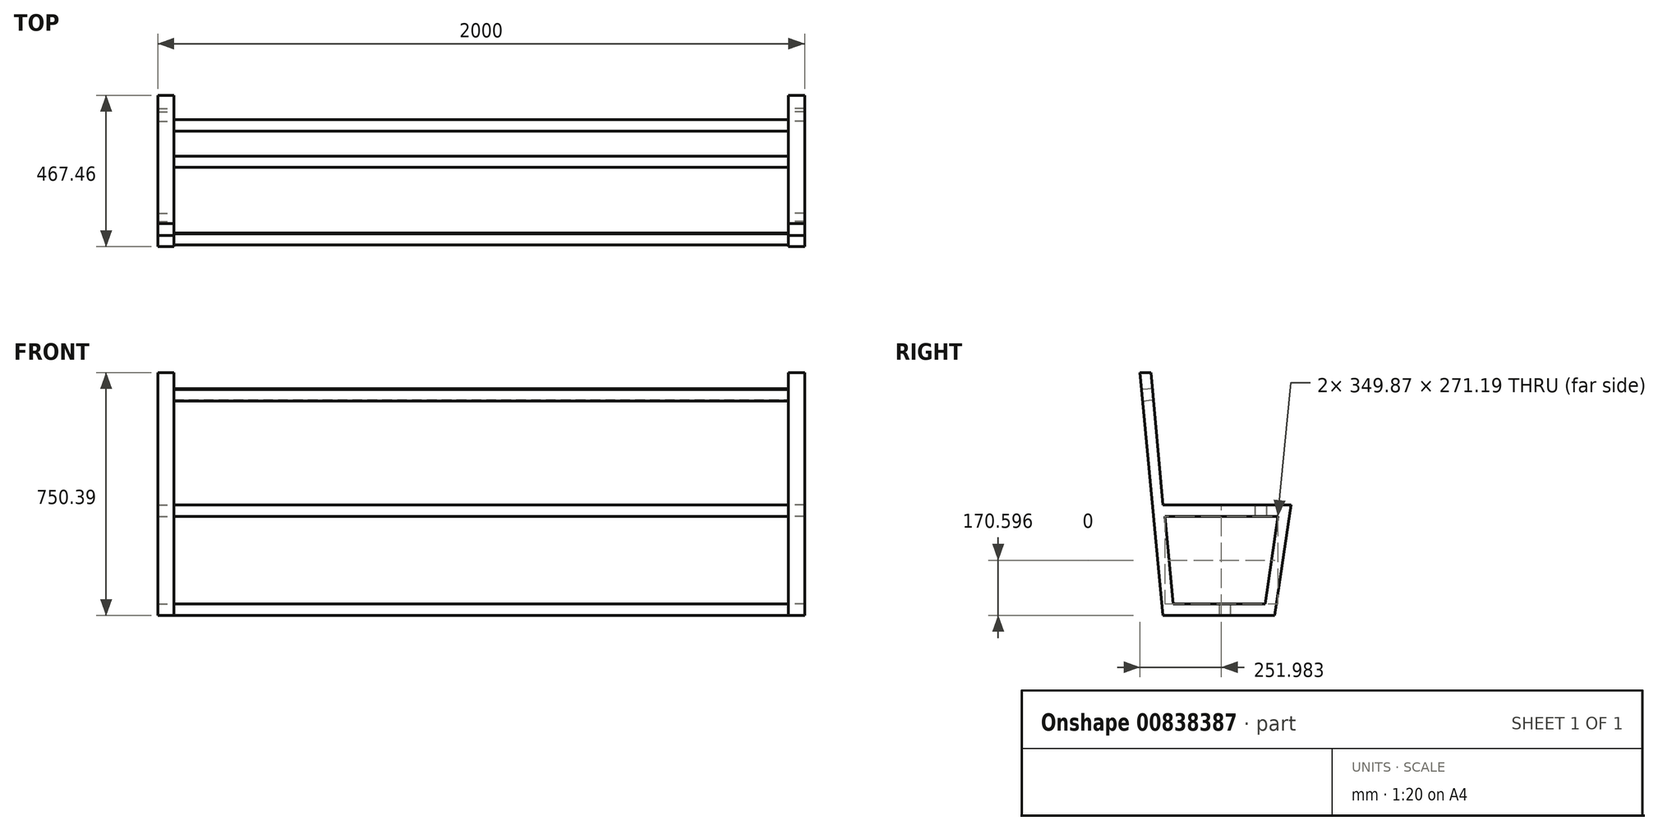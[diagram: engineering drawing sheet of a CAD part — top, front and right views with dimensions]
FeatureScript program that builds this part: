
annotation { "Feature Type Name" : "Feature", "Feature Type Description" : "" }
export const myFeature = defineFeature(function(context is Context, id is Id, definition is map)
    precondition{}
    {
        {
            var Q0;
            Q0=qCreatedBy(makeId("Right.planeOp"),FACE);
            var sketch = newSketch(context, id + "F0", { "sketchPlane" : qUnion([Q0])});
            skLineSegment(sketch, "E0.top", {"start": v(32.57, 750.39) * mm, "end": v(66.99, 750.39) * mm});
            skLineSegment(sketch, "E1", {"start": v(66.99, 750.39) * mm, "end": v(103.34, 341.2) * mm});
            skLineSegment(sketch, "E2", {"start": v(103.34, 341.2) * mm, "end": v(500.03, 341.2) * mm});
            skLineSegment(sketch, "E3", {"start": v(32.57, 750.39) * mm, "end": v(103.34, 0) * mm});
            skLineSegment(sketch, "E4", {"start": v(103.34, 0) * mm, "end": v(449.66, 0) * mm});
            skLineSegment(sketch, "E5", {"start": v(449.66, 0) * mm, "end": v(500.03, 341.2) * mm});
            skLineSegment(sketch, "E6", {"start": v(135.2, 35) * mm, "end": v(419.45, 35) * mm});
            skLineSegment(sketch, "E7", {"start": v(419.45, 35) * mm, "end": v(459.49, 306.2) * mm});
            skLineSegment(sketch, "E8", {"start": v(459.49, 306.2) * mm, "end": v(109.62, 306.2) * mm});
            skLineSegment(sketch, "E9", {"start": v(109.62, 306.2) * mm, "end": v(135.2, 35) * mm});
            skSolve(sketch);
        }
        {
            var Q0;
            Q0 = qSketchRegion(id + "F0", true);
            extrude(context, id + "F1", {"entities" : qUnion([Q0]), "depth" : 50 * mm, "offsetDistance" : 25 * mm});
        }
        {
            var Q0;
            Q0=makeQuery(id+"F1.opExtrude","CAP_FACE",FACE,{"disambiguationData":[OSD([sQuery(id+"F0.wireOp",EDGE,"E0.top"),sQuery(id+"F0.wireOp",EDGE,"E1"),sQuery(id+"F0.wireOp",EDGE,"E2"),sQuery(id+"F0.wireOp",EDGE,"E3"),sQuery(id+"F0.wireOp",EDGE,"E4"),sQuery(id+"F0.wireOp",EDGE,"E5"),sQuery(id+"F0.wireOp",EDGE,"E6"),sQuery(id+"F0.wireOp",EDGE,"E7"),sQuery(id+"F0.wireOp",EDGE,"E8"),sQuery(id+"F0.wireOp",EDGE,"E9")])],"isStart":true});
            var sketch = newSketch(context, id + "F2", { "sketchPlane" : qUnion([Q0])});
            skLineSegment(sketch, "E10.bottom", {"start": v(-284.55, 306.2) * mm, "end": v(-319.55, 306.2) * mm});
            skLineSegment(sketch, "E10.top", {"start": v(-284.55, 341.2) * mm, "end": v(-319.55, 341.2) * mm});
            skLineSegment(sketch, "E10.left", {"start": v(-284.55, 306.2) * mm, "end": v(-284.55, 341.2) * mm});
            skLineSegment(sketch, "E10.right", {"start": v(-319.55, 306.2) * mm, "end": v(-319.55, 341.2) * mm});
            skLineSegment(sketch, "E11.bottom", {"start": v(-277.32, 35) * mm, "end": v(-312.32, 35) * mm});
            skLineSegment(sketch, "E11.top", {"start": v(-277.32, 0) * mm, "end": v(-312.32, 0) * mm});
            skLineSegment(sketch, "E11.left", {"start": v(-277.32, 35) * mm, "end": v(-277.32, 0) * mm});
            skLineSegment(sketch, "E11.right", {"start": v(-312.32, 35) * mm, "end": v(-312.32, 0) * mm});
            skSolve(sketch);
        }
        {
            var Q0;
            Q0 = qSketchRegion(id + "F2", true);
            extrude(context, id + "F3", {"entities" : qUnion([Q0]), "depth" : 950 * mm, "offsetDistance" : 25 * mm});
        }
        {
            var Q0;
            Q0=makeQuery(id+"F1.opExtrude","SWEPT_BODY",BODY,{"disambiguationData":[OSD([sQuery(id+"F0.wireOp",EDGE,"E0.top"),sQuery(id+"F0.wireOp",EDGE,"E1"),sQuery(id+"F0.wireOp",EDGE,"E2"),sQuery(id+"F0.wireOp",EDGE,"E3"),sQuery(id+"F0.wireOp",EDGE,"E4"),sQuery(id+"F0.wireOp",EDGE,"E5"),sQuery(id+"F0.wireOp",EDGE,"E6"),sQuery(id+"F0.wireOp",EDGE,"E7"),sQuery(id+"F0.wireOp",EDGE,"E8"),sQuery(id+"F0.wireOp",EDGE,"E9")])]});
            var Q1;
            Q1=makeQuery(id+"F3.opExtrude","CAP_FACE",FACE,{"disambiguationData":[OSD([sQuery(id+"F2.wireOp",EDGE,"E10.bottom"),sQuery(id+"F2.wireOp",EDGE,"E10.top"),sQuery(id+"F2.wireOp",EDGE,"E10.left"),sQuery(id+"F2.wireOp",EDGE,"E10.right")])],"isStart":false});
            mirror(context, id + "F4", {"entities" : qUnion([Q0]), "mirrorPlane" : qUnion([Q1])});
        }
        {
            var Q0;
            Q0=makeQuery(id+"F3.opExtrude","SWEPT_BODY",BODY,{"disambiguationData":[OSD([sQuery(id+"F2.wireOp",EDGE,"E11.bottom"),sQuery(id+"F2.wireOp",EDGE,"E11.top"),sQuery(id+"F2.wireOp",EDGE,"E11.left"),sQuery(id+"F2.wireOp",EDGE,"E11.right")])]});
            var Q1;
            Q1=makeQuery(id+"F3.opExtrude","SWEPT_BODY",BODY,{"disambiguationData":[OSD([sQuery(id+"F2.wireOp",EDGE,"E10.bottom"),sQuery(id+"F2.wireOp",EDGE,"E10.top"),sQuery(id+"F2.wireOp",EDGE,"E10.left"),sQuery(id+"F2.wireOp",EDGE,"E10.right")])]});
            deleteBodies(context, id + "F5", {"entities" : qUnion([Q0, Q1])});
        }
        {
            var Q0;
            Q0=makeQuery(id+"F1.opExtrude","CAP_FACE",FACE,{"disambiguationData":[OSD([sQuery(id+"F0.wireOp",EDGE,"E0.top"),sQuery(id+"F0.wireOp",EDGE,"E1"),sQuery(id+"F0.wireOp",EDGE,"E2"),sQuery(id+"F0.wireOp",EDGE,"E3"),sQuery(id+"F0.wireOp",EDGE,"E4"),sQuery(id+"F0.wireOp",EDGE,"E5"),sQuery(id+"F0.wireOp",EDGE,"E6"),sQuery(id+"F0.wireOp",EDGE,"E7"),sQuery(id+"F0.wireOp",EDGE,"E8"),sQuery(id+"F0.wireOp",EDGE,"E9")])],"isStart":true});
            var sketch = newSketch(context, id + "F6", { "sketchPlane" : qUnion([Q0])});
            skLineSegment(sketch, "E12.bottom", {"start": v(-277.32, 35) * mm, "end": v(-312.32, 35) * mm});
            skLineSegment(sketch, "E12.top", {"start": v(-277.32, 0) * mm, "end": v(-312.32, 0) * mm});
            skLineSegment(sketch, "E12.left", {"start": v(-277.32, 35) * mm, "end": v(-277.32, 0) * mm});
            skLineSegment(sketch, "E12.right", {"start": v(-312.32, 35) * mm, "end": v(-312.32, 0) * mm});
            skLineSegment(sketch, "E13", {"start": v(-71.37, 701.06) * mm, "end": v(-37.5, 698.05) * mm});
            skLineSegment(sketch, "E14", {"start": v(-37.5, 698.05) * mm, "end": v(-40.8, 663.2) * mm});
            skLineSegment(sketch, "E15", {"start": v(-40.8, 663.2) * mm, "end": v(-74.45, 666.38) * mm});
            skLineSegment(sketch, "E16", {"start": v(-74.45, 666.38) * mm, "end": v(-71.37, 701.06) * mm});
            skLineSegment(sketch, "E17.bottom", {"start": v(-424.8, 306.2) * mm, "end": v(-389.8, 306.2) * mm});
            skLineSegment(sketch, "E17.top", {"start": v(-424.8, 341.2) * mm, "end": v(-389.8, 341.2) * mm});
            skLineSegment(sketch, "E17.left", {"start": v(-424.8, 306.2) * mm, "end": v(-424.8, 341.2) * mm});
            skLineSegment(sketch, "E17.right", {"start": v(-389.8, 306.2) * mm, "end": v(-389.8, 341.2) * mm});
            skSolve(sketch);
        }
        {
            var Q0;
            Q0 = qSketchRegion(id + "F6", true);
            extrude(context, id + "F7", {"entities" : qUnion([Q0]), "endBound" : BoundingType.UP_TO_NEXT, "depth" : 25 * mm, "offsetDistance" : 25 * mm});
        }
    });
